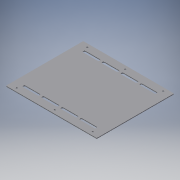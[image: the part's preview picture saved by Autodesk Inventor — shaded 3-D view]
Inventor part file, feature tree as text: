
AUTODESK INVENTOR PART (.ipt)
format: ipt  version: 2018 (Build 220112000, 112)  size: 247,296 bytes
history: native  units: mm
features: other x3, sketch x2, fillet x1, extrude x1, projected_geometry x1
ambient origin geometry x8: Origin, YZ Plane, XZ Plane, XY Plane, X Axis, Y Axis, Z Axis, Center Point
bodies: Volumenkörper1 (feature_tree)
feature tree (8):
  other  "Fläche1"
  fillet  "Rundung1"  Radius=263.0mm
  extrude  "Extrusion1"  Depth=224.0mm
  sketch  "Skizze1"  dims[d1=224.0mm d2=4.3mm]
  other  "Grobblech1"
  sketch  "Skizze2"  dims[d3=0.0mm d4=10.0mm d5=4.3mm d6=4.3mm d7=10.0mm d8=10.0mm d9=110.0mm d10=110.0mm d11=2.0mm d12=2.0mm d13=25.0mm d14=110.0mm d15=48.0mm d16=7.0mm d17=3.5mm d18=48.0mm d19=7.0mm d20=7.0mm d21=3.5mm d22=10.0mm d23=0.0mm]
  projected_geometry  "Projizierte Kontur1"
  other  "Definition1"
